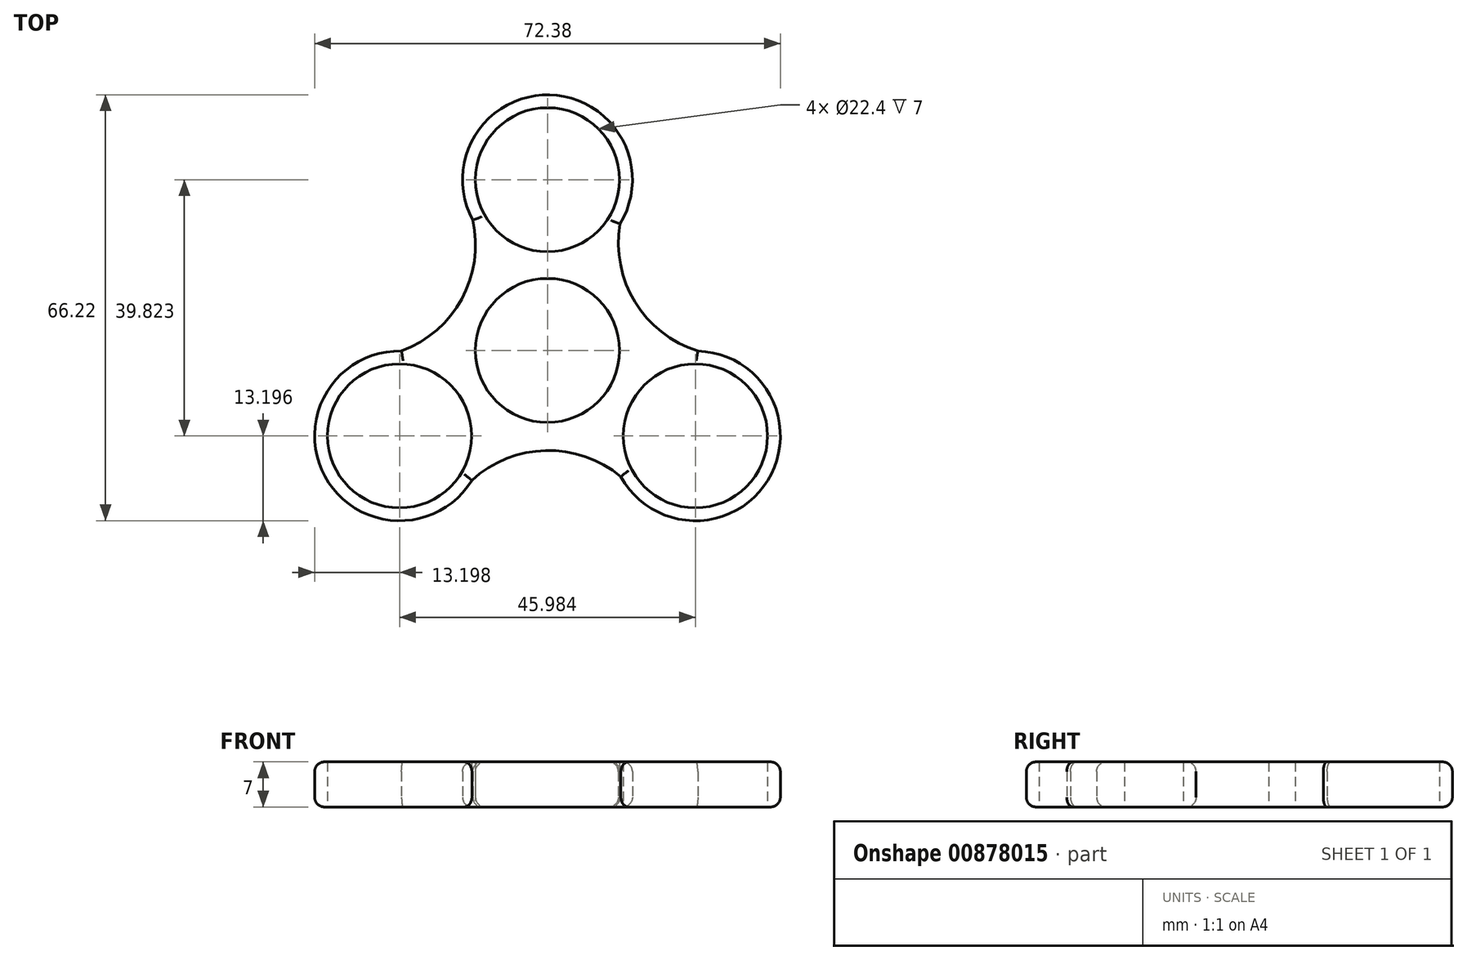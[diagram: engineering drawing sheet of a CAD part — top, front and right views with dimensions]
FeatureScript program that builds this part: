
annotation { "Feature Type Name" : "Feature", "Feature Type Description" : "" }
export const myFeature = defineFeature(function(context is Context, id is Id, definition is map)
    precondition{}
    {
        {
            var Q0;
            Q0=qCreatedBy(makeId("Top.planeOp"),FACE);
            var sketch = newSketch(context, id + "F0", { "sketchPlane" : qUnion([Q0])});
            skCircle(sketch, "E0", {"center": v(0, 0) * mm, "radius": 11.2 * mm});
            skCircle(sketch, "E1", {"center": v(0, 26.55) * mm, "radius": 11.2 * mm});
            skArc(sketch, "E2", {"start": v(11.28, 19.69) * mm, "mid": v(0.34, 39.74) * mm, "end": v(-11.61, 20.28) * mm});
            skArc(sketch, "E3.1.0", {"start": v(-22.69, -0.08) * mm, "mid": v(-34.59, -19.58) * mm, "end": v(-11.75, -20.2) * mm});
            skCircle(sketch, "E3.1.1", {"center": v(-23, -13.27) * mm, "radius": 11.2 * mm});
            skArc(sketch, "E3.2.0", {"start": v(11.41, -19.6) * mm, "mid": v(34.25, -20.17) * mm, "end": v(23.37, -0.08) * mm});
            skCircle(sketch, "E3.2.1", {"center": v(23, -13.27) * mm, "radius": 11.2 * mm});
            skLineSegment(sketch, "E4", {"start": v(-11.43, -6.6) * mm, "end": v(-9.7, -5.6) * mm, "construction": true});
            skArc(sketch, "E5", {"start": v(11.28, 19.69) * mm, "mid": v(13.61, 7.53) * mm, "end": v(23.37, -0.08) * mm});
            skPoint(sketch, "E5.endSnap0", {"position": v(23.37, 13.5) * mm});
            skArc(sketch, "E6.1.0", {"start": v(-22.69, -0.08) * mm, "mid": v(-13.33, 8.02) * mm, "end": v(-11.61, 20.28) * mm});
            skArc(sketch, "E6.2.0", {"start": v(11.41, -19.6) * mm, "mid": v(-0.28, -15.55) * mm, "end": v(-11.75, -20.2) * mm});
            skPoint(sketch, "E7.orphan", {"position": v(69.73, 40.26) * mm});
            skLineSegment(sketch, "E8.trimOffspring", {"start": v(9.7, 5.6) * mm, "end": v(11.43, 6.6) * mm, "construction": true});
            skSolve(sketch);
        }
        {
            var Q0;
            Q0=makeQuery(id+"F0.imprint","IMPRINT",FACE,{"disambiguationData":[TD([[makeQuery(id+"F0.imprint","IMPRINT",EDGE,{"derivedFrom":sQuery(id+"F0.wireOp",EDGE,"E0")}),-1.0]])]});
            extrude(context, id + "F1", {"entities" : qUnion([Q0]), "depth" : 7 * mm, "offsetDistance" : 25 * mm});
        }
        {
            var Q0;
            Q0=makeQuery(id+"F1.opExtrude","CAP_EDGE",EDGE,{"disambiguationData":[OSD([sQuery(id+"F0.wireOp",EDGE,"E6.2.0")])],"isStart":false});
            var Q1;
            Q1=makeQuery(id+"F1.opExtrude","CAP_EDGE",EDGE,{"disambiguationData":[OSD([sQuery(id+"F0.wireOp",EDGE,"E6.2.0")])],"isStart":true});
            var Q2;
            Q2=makeQuery(id+"F1.opExtrude","CAP_EDGE",EDGE,{"disambiguationData":[OSD([sQuery(id+"F0.wireOp",EDGE,"E3.1.0")])],"isStart":false});
            var Q3;
            Q3=makeQuery(id+"F1.opExtrude","CAP_EDGE",EDGE,{"disambiguationData":[OSD([sQuery(id+"F0.wireOp",EDGE,"E6.1.0")])],"isStart":false});
            var Q4;
            Q4=makeQuery(id+"F1.opExtrude","CAP_EDGE",EDGE,{"disambiguationData":[OSD([sQuery(id+"F0.wireOp",EDGE,"E2")])],"isStart":false});
            var Q5;
            Q5=makeQuery(id+"F1.opExtrude","CAP_EDGE",EDGE,{"disambiguationData":[OSD([sQuery(id+"F0.wireOp",EDGE,"E5")])],"isStart":false});
            var Q6;
            Q6=makeQuery(id+"F1.opExtrude","CAP_EDGE",EDGE,{"disambiguationData":[OSD([sQuery(id+"F0.wireOp",EDGE,"E3.2.0")])],"isStart":false});
            fillet(context, id + "F2", {"entities" : qUnion([Q0, Q1, Q2, Q3, Q4, Q5, Q6]), "radius" : 1.5 * mm, "tangentPropagation" : true, "allowEdgeOverflow" : false});
        }
        {
            var Q0;
            Q0=makeQuery(id+"F1.opExtrude","CAP_EDGE",EDGE,{"disambiguationData":[OSD([sQuery(id+"F0.wireOp",EDGE,"E3.1.0")])],"isStart":true});
            var Q1;
            {var subQ0=sQuery(id+"F0.wireOp",EDGE,"E6.2.0");Q1=makeQuery(id+"F2.opFillet","BLEND_EDGE",EDGE,{"blendedFrom":[makeQuery(id+"F1.opExtrude","CAP_EDGE",EDGE,{"disambiguationData":[OSD([subQ0])],"isStart":true}),makeQuery(id+"F1.opExtrude","CAP_FACE",FACE,{"disambiguationData":[OSD([sQuery(id+"F0.wireOp",EDGE,"E0"),sQuery(id+"F0.wireOp",EDGE,"E1"),sQuery(id+"F0.wireOp",EDGE,"E2"),sQuery(id+"F0.wireOp",EDGE,"E3.1.0"),sQuery(id+"F0.wireOp",EDGE,"E3.1.1"),sQuery(id+"F0.wireOp",EDGE,"E3.2.0"),sQuery(id+"F0.wireOp",EDGE,"E3.2.1"),sQuery(id+"F0.wireOp",EDGE,"E5"),sQuery(id+"F0.wireOp",EDGE,"E6.1.0"),subQ0])],"isStart":true})],"blendedInto":[makeQuery(id+"F1.opExtrude","CAP_FACE",FACE,{"disambiguationData":[OSD([sQuery(id+"F0.wireOp",EDGE,"E0"),sQuery(id+"F0.wireOp",EDGE,"E1"),sQuery(id+"F0.wireOp",EDGE,"E2"),sQuery(id+"F0.wireOp",EDGE,"E3.1.0"),sQuery(id+"F0.wireOp",EDGE,"E3.1.1"),sQuery(id+"F0.wireOp",EDGE,"E3.2.0"),sQuery(id+"F0.wireOp",EDGE,"E3.2.1"),sQuery(id+"F0.wireOp",EDGE,"E5"),sQuery(id+"F0.wireOp",EDGE,"E6.1.0"),subQ0])],"isStart":true})]});}
            var Q2;
            Q2=makeQuery(id+"F1.opExtrude","CAP_EDGE",EDGE,{"disambiguationData":[OSD([sQuery(id+"F0.wireOp",EDGE,"E3.2.0")])],"isStart":true});
            var Q3;
            Q3=makeQuery(id+"F1.opExtrude","CAP_EDGE",EDGE,{"disambiguationData":[OSD([sQuery(id+"F0.wireOp",EDGE,"E5")])],"isStart":true});
            var Q4;
            Q4=makeQuery(id+"F1.opExtrude","CAP_EDGE",EDGE,{"disambiguationData":[OSD([sQuery(id+"F0.wireOp",EDGE,"E2")])],"isStart":true});
            var Q5;
            Q5=makeQuery(id+"F1.opExtrude","CAP_EDGE",EDGE,{"disambiguationData":[OSD([sQuery(id+"F0.wireOp",EDGE,"E6.1.0")])],"isStart":true});
            fillet(context, id + "F3", {"entities" : qUnion([Q0, Q1, Q2, Q3, Q4, Q5]), "radius" : 1.5 * mm, "tangentPropagation" : true, "allowEdgeOverflow" : false});
        }
    });
